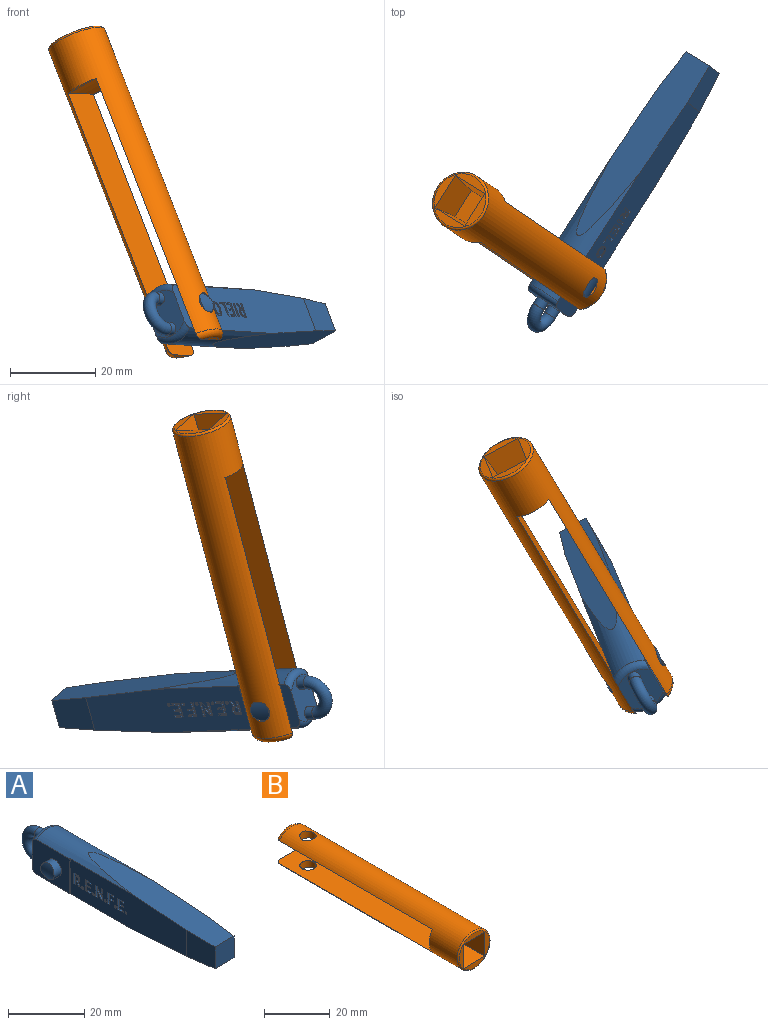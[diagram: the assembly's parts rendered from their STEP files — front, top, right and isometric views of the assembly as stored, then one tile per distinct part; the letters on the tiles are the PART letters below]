
ASSEMBLY  parts=2 mates=1
PART A: 277 faces, bbox 14x74.8x15.2 mm
  f0: plane 42.99x11.2mm, normal (-1,0,0), area 431.2mm2, adj f2,f3,f6,f10,f11,f12,f125,f126
  f1: plane 42.99x11.2mm, normal (1,0,0), area 436.1mm2, adj f2,f3,f7,f9,f10,f12,f18,f19
  f2: cylinder r=7mm len=35.47mm, axis (0,-1,0), area 201.7mm2, adj f0,f1,f5,f6,f7,f8,f12,f16
  f3: cylinder r=7mm len=35.47mm, axis (0,-1,0), area 201.7mm2, adj f0,f1,f5,f6,f7,f8,f10,f17
  f4: plane 11x8.5mm, normal (0,1,0), area 69mm2, adj f5,f8,f16,f17,f274,f275
  f5: plane 14x11.12mm, normal (-1,0,0), area 134.8mm2, adj f2,f3,f4,f6,f15,f16,f17
  f6: plane 11.2x0.05mm, normal (0,-1,0), area 0.6mm2, adj f0,f2,f3,f5
  f7: plane 11.2x0.05mm, normal (0,-1,0), area 0.6mm2, adj f1,f2,f3,f8
  f8: plane 14x11.12mm, normal (1,0,0), area 134.8mm2, adj f2,f3,f4,f7,f14,f16,f17
  f9: plane 10.01x8.4mm, normal (1,-0.07,0), area 77.3mm2, adj f1,f10,f12,f13
  f10: plane 50.05x8.4mm, normal (0,-0.07,1), area 360.7mm2, adj f0,f1,f3,f9,f11,f13
  f11: plane 10.01x8.4mm, normal (-1,-0.07,0), area 77.3mm2, adj f0,f10,f12,f13
  f12: plane 50.05x8.4mm, normal (0,-0.07,-1), area 360.7mm2, adj f0,f1,f2,f9,f11,f13
  f13: plane 7x7mm, normal (0,-1,0), area 49mm2, adj f9,f10,f11,f12
  f14: cylinder r=2.5mm len=5mm, axis (-1,0,0), area 39.6mm2, adj f8,f273
  f15: cylinder r=2.5mm len=5mm, axis (-1,0,0), area 39.6mm2, adj f5,f272
  f16: torus R=5.5mm, axis (0,-1,0), area 21.9mm2, adj f2,f4,f5,f8
  f17: torus R=5.5mm, axis (0,-1,0), area 21.9mm2, adj f3,f4,f5,f8
  f18: plane 1.41x0.5mm, normal (0,0,-1), area 0.7mm2, adj f1,f19,f21,f22
  f19: plane 0.5x0.43mm, normal (0,1,0), area 0.2mm2, adj f1,f18,f20,f22
  f20: plane 1.41x0.5mm, normal (0,0,1), area 0.7mm2, adj f1,f19,f21,f22
  f21: plane 0.5x0.43mm, normal (0,-1,0), area 0.2mm2, adj f1,f18,f20,f22
  f22: plane 1.41x0.43mm, normal (1,0,0), area 0.6mm2, adj f18,f19,f20,f21
  f23: extruded ~0.55x0.5mm, area 0.3mm2, adj f1,f24,f42,f43
  f24: extruded ~0.75x0.5mm, area 0.4mm2, adj f1,f23,f25,f43
  f25: extruded ~0.5x0.02mm, area 0mm2, adj f1,f24,f26,f43
  f26: extruded ~0.73x0.5mm, area 0.4mm2, adj f1,f25,f27,f43
  f27: extruded ~0.55x0.5mm, area 0.3mm2, adj f1,f26,f28,f43
  f28: extruded ~0.5x0.43mm, area 0.3mm2, adj f1,f27,f29,f43
  f29: extruded ~0.54x0.5mm, area 0.3mm2, adj f1,f28,f30,f43
  f30: plane 0.5x0.47mm, normal (0,-1,0), area 0.2mm2, adj f1,f29,f31,f43
  f31: extruded ~0.5x0.3mm, area 0.2mm2, adj f1,f30,f32,f43
  f32: extruded ~0.5x0.25mm, area 0.2mm2, adj f1,f31,f33,f43
  f33: extruded ~0.5x0.4mm, area 0.2mm2, adj f1,f32,f34,f43
  f34: extruded ~0.56x0.5mm, area 0.3mm2, adj f1,f33,f35,f43
  f35: extruded ~0.5x0.02mm, area 0mm2, adj f1,f34,f36,f43
  f36: extruded ~0.57x0.5mm, area 0.3mm2, adj f1,f35,f37,f43
  f37: extruded ~0.5x0.4mm, area 0.2mm2, adj f1,f36,f38,f43
  f38: extruded ~0.5x0.25mm, area 0.2mm2, adj f1,f37,f39,f43
  f39: extruded ~0.5x0.3mm, area 0.2mm2, adj f1,f38,f40,f43
  f40: plane 0.5x0.47mm, normal (0,-1,0), area 0.2mm2, adj f1,f39,f41,f43
  f41: extruded ~0.54x0.5mm, area 0.3mm2, adj f1,f40,f42,f43
  f42: extruded ~0.5x0.43mm, area 0.3mm2, adj f1,f23,f41,f43
  f43: plane 3.57x1.36mm, normal (1,0,0), area 2.3mm2, adj f23,f24,f25,f26,f27,f28,f29,f30
  f44: plane 3.07x0.5mm, normal (0,-1,0), area 1.5mm2, adj f1,f45,f49,f50
  f45: plane 0.58x0.5mm, normal (0,0,-1), area 0.3mm2, adj f1,f44,f46,f50
  f46: plane 3.5x0.5mm, normal (0,1,0), area 1.7mm2, adj f1,f45,f47,f50
  f47: plane 2.19x0.5mm, normal (0,0,1), area 1.1mm2, adj f1,f46,f48,f50
  f48: plane 0.5x0.43mm, normal (0,-1,0), area 0.2mm2, adj f1,f47,f49,f50
  f49: plane 1.61x0.5mm, normal (0,0,-1), area 0.8mm2, adj f1,f44,f48,f50
  f50: plane 3.5x2.19mm, normal (1,0,0), area 2.7mm2, adj f44,f45,f46,f47,f48,f49
  f51: plane 0.5x0.39mm, normal (0,1,0), area 0.2mm2, adj f1,f52,f54,f55
  f52: plane 1.27x0.5mm, normal (0,0,1), area 0.6mm2, adj f1,f51,f53,f55
  f53: plane 0.5x0.39mm, normal (0,-1,0), area 0.2mm2, adj f1,f52,f54,f55
  f54: plane 1.27x0.5mm, normal (0,0,-1), area 0.6mm2, adj f1,f51,f53,f55
  f55: plane 1.27x0.39mm, normal (1,0,0), area 0.5mm2, adj f51,f52,f53,f54
  f56: plane 3.5x0.5mm, normal (0,-1,0), area 1.7mm2, adj f1,f57,f59,f60
  f57: plane 0.58x0.5mm, normal (0,0,-1), area 0.3mm2, adj f1,f56,f58,f60
  f58: plane 3.5x0.5mm, normal (0,1,0), area 1.7mm2, adj f1,f57,f59,f60
  f59: plane 0.58x0.5mm, normal (0,0,1), area 0.3mm2, adj f1,f56,f58,f60
  f60: plane 3.5x0.58mm, normal (1,0,0), area 2mm2, adj f56,f57,f58,f59
  f61: plane 0.5x0.43mm, normal (0,-1,0), area 0.2mm2, adj f1,f62,f64,f65
  f62: plane 1.41x0.5mm, normal (0,0,-1), area 0.7mm2, adj f1,f61,f63,f65
  f63: plane 0.5x0.43mm, normal (0,1,0), area 0.2mm2, adj f1,f62,f64,f65
  f64: plane 1.41x0.5mm, normal (0,0,1), area 0.7mm2, adj f1,f61,f63,f65
  f65: plane 1.41x0.43mm, normal (1,0,0), area 0.6mm2, adj f61,f62,f63,f64
  f66: plane 3.5x0.5mm, normal (0,-1,0), area 1.7mm2, adj f1,f67,f69,f70
  f67: plane 0.57x0.5mm, normal (0,0,-1), area 0.3mm2, adj f1,f66,f68,f70
  f68: plane 3.5x0.5mm, normal (0,1,0), area 1.7mm2, adj f1,f67,f69,f70
  f69: plane 0.57x0.5mm, normal (0,0,1), area 0.3mm2, adj f1,f66,f68,f70
  f70: plane 3.5x0.57mm, normal (1,0,0), area 2mm2, adj f66,f67,f68,f69
  f71: extruded ~0.5x0.03mm, area 0mm2, adj f1,f72,f97,f98
  f72: plane 1.27x0.66mm, normal (0,0.89,0.46), area 0.7mm2, adj f1,f71,f73,f98
  f73: plane 0.6x0.5mm, normal (0,0,1), area 0.3mm2, adj f1,f72,f74,f98
  f74: plane 1.38x0.8mm, normal (0,-0.87,-0.5), area 0.8mm2, adj f1,f73,f75,f98
  f75: extruded ~0.5x0.46mm, area 0.3mm2, adj f1,f74,f76,f98
  f76: extruded ~0.5x0.02mm, area 0mm2, adj f1,f75,f77,f98
  f77: extruded ~0.65x0.5mm, area 0.3mm2, adj f1,f76,f78,f98
  f78: extruded ~0.5x0.45mm, area 0.2mm2, adj f1,f77,f79,f98
  f79: extruded ~0.5x0.34mm, area 0.2mm2, adj f1,f78,f80,f98
  f80: extruded ~0.5x0.39mm, area 0.2mm2, adj f1,f79,f81,f98
  f81: extruded ~0.5x0.44mm, area 0.2mm2, adj f1,f80,f82,f98
  f82: plane 0.5x0.24mm, normal (0,0,-1), area 0.1mm2, adj f1,f81,f83,f98
  f83: plane 0.5x0.43mm, normal (0,1,0), area 0.2mm2, adj f1,f82,f84,f98
  f84: plane 0.5x0.23mm, normal (0,0,1), area 0.1mm2, adj f1,f83,f85,f98
  f85: extruded ~0.5x0.35mm, area 0.2mm2, adj f1,f84,f86,f98
  f86: extruded ~0.5x0.21mm, area 0.1mm2, adj f1,f85,f87,f98
  f87: extruded ~0.5x0.21mm, area 0.1mm2, adj f1,f86,f88,f98
  f88: extruded ~0.5x0.2mm, area 0.1mm2, adj f1,f87,f89,f98
  f89: extruded ~0.5x0.36mm, area 0.2mm2, adj f1,f88,f90,f98
  f90: extruded ~0.5x0.23mm, area 0.1mm2, adj f1,f89,f91,f98
  f91: extruded ~0.5x0.11mm, area 0.1mm2, adj f1,f90,f92,f98
  f92: extruded ~0.5x0.08mm, area 0mm2, adj f1,f91,f93,f98
  f93: extruded ~0.5x0.21mm, area 0.1mm2, adj f1,f92,f94,f98
  f94: plane 0.5x0.32mm, normal (0,0,-1), area 0.2mm2, adj f1,f93,f95,f98
  f95: plane 0.5x0.42mm, normal (0,1,0), area 0.2mm2, adj f1,f94,f96,f98
  f96: plane 0.5x0.27mm, normal (0,0,1), area 0.1mm2, adj f1,f95,f97,f98
  f97: extruded ~0.5x0.05mm, area 0mm2, adj f1,f71,f96,f98
  f98: plane 3.5x1.61mm, normal (1,0,0), area 2.4mm2, adj f71,f72,f73,f74,f75,f76,f77,f78
  f99: plane 3.5x0.5mm, normal (0,1,0), area 1.7mm2, adj f1,f100,f102,f103
  f100: plane 0.58x0.5mm, normal (0,0,1), area 0.3mm2, adj f1,f99,f101,f103
  f101: plane 3.5x0.5mm, normal (0,-1,0), area 1.7mm2, adj f1,f100,f102,f103
  f102: plane 0.58x0.5mm, normal (0,0,-1), area 0.3mm2, adj f1,f99,f101,f103
  f103: plane 3.5x0.58mm, normal (1,0,0), area 2mm2, adj f99,f100,f101,f102
  f104: extruded ~0.55x0.5mm, area 0.3mm2, adj f1,f105,f123,f124
  f105: extruded ~0.5x0.43mm, area 0.3mm2, adj f1,f104,f106,f124
  f106: extruded ~0.54x0.5mm, area 0.3mm2, adj f1,f105,f107,f124
  f107: plane 0.5x0.47mm, normal (0,1,0), area 0.2mm2, adj f1,f106,f108,f124
  f108: extruded ~0.5x0.3mm, area 0.2mm2, adj f1,f107,f109,f124
  f109: extruded ~0.5x0.25mm, area 0.2mm2, adj f1,f108,f110,f124
  f110: extruded ~0.5x0.4mm, area 0.2mm2, adj f1,f109,f111,f124
  f111: extruded ~0.58x0.5mm, area 0.3mm2, adj f1,f110,f112,f124
  f112: extruded ~0.5x0.02mm, area 0mm2, adj f1,f111,f113,f124
  f113: extruded ~0.56x0.5mm, area 0.3mm2, adj f1,f112,f114,f124
  f114: extruded ~0.5x0.4mm, area 0.2mm2, adj f1,f113,f115,f124
  f115: extruded ~0.5x0.25mm, area 0.2mm2, adj f1,f114,f116,f124
  f116: extruded ~0.5x0.3mm, area 0.2mm2, adj f1,f115,f117,f124
  f117: plane 0.5x0.47mm, normal (0,1,0), area 0.2mm2, adj f1,f116,f118,f124
  f118: extruded ~0.54x0.5mm, area 0.3mm2, adj f1,f117,f119,f124
  f119: extruded ~0.5x0.43mm, area 0.3mm2, adj f1,f118,f120,f124
  f120: extruded ~0.55x0.5mm, area 0.3mm2, adj f1,f119,f121,f124
  f121: extruded ~0.73x0.5mm, area 0.4mm2, adj f1,f120,f122,f124
  f122: extruded ~0.5x0.02mm, area 0mm2, adj f1,f121,f123,f124
  f123: extruded ~0.75x0.5mm, area 0.4mm2, adj f1,f104,f122,f124
  f124: plane 3.57x1.36mm, normal (1,0,0), area 2.2mm2, adj f104,f105,f106,f107,f108,f109,f110,f111
  f125: extruded ~0.5x0.24mm, area 0.1mm2, adj f0,f126,f132,f133
  f126: extruded ~0.5x0.24mm, area 0.1mm2, adj f0,f125,f127,f133
  f127: extruded ~0.5x0.24mm, area 0.1mm2, adj f0,f126,f128,f133
  f128: extruded ~0.5x0.24mm, area 0.1mm2, adj f0,f127,f129,f133
  f129: extruded ~0.5x0.24mm, area 0.1mm2, adj f0,f128,f130,f133
  f130: extruded ~0.5x0.24mm, area 0.1mm2, adj f0,f129,f131,f133
  f131: extruded ~0.5x0.24mm, area 0.1mm2, adj f0,f130,f132,f133
  f132: extruded ~0.5x0.24mm, area 0.1mm2, adj f0,f125,f131,f133
  f133: plane 0.68x0.68mm, normal (-1,0,0), area 0.4mm2, adj f125,f126,f127,f128,f129,f130,f131,f132
  f134: plane 0.5x0.39mm, normal (0,-1,0), area 0.2mm2, adj f0,f135,f137,f138
  f135: plane 1.27x0.5mm, normal (0,0,1), area 0.6mm2, adj f0,f134,f136,f138
  f136: plane 0.5x0.39mm, normal (0,1,0), area 0.2mm2, adj f0,f135,f137,f138
  f137: plane 1.27x0.5mm, normal (0,0,-1), area 0.6mm2, adj f0,f134,f136,f138
  f138: plane 1.27x0.39mm, normal (-1,0,0), area 0.5mm2, adj f134,f135,f136,f137
  f139: plane 3.5x0.5mm, normal (0,1,0), area 1.7mm2, adj f0,f140,f142,f143
  f140: plane 0.58x0.5mm, normal (0,0,-1), area 0.3mm2, adj f0,f139,f141,f143
  f141: plane 3.5x0.5mm, normal (0,-1,0), area 1.7mm2, adj f0,f140,f142,f143
  f142: plane 0.58x0.5mm, normal (0,0,1), area 0.3mm2, adj f0,f139,f141,f143
  f143: plane 3.5x0.58mm, normal (-1,0,0), area 2mm2, adj f139,f140,f141,f142
  f144: plane 0.5x0.39mm, normal (0,-1,0), area 0.2mm2, adj f0,f145,f147,f148
  f145: plane 1.27x0.5mm, normal (0,0,1), area 0.6mm2, adj f0,f144,f146,f148
  f146: plane 0.5x0.39mm, normal (0,1,0), area 0.2mm2, adj f0,f145,f147,f148
  f147: plane 1.27x0.5mm, normal (0,0,-1), area 0.6mm2, adj f0,f144,f146,f148
  f148: plane 1.27x0.39mm, normal (-1,0,0), area 0.5mm2, adj f144,f145,f146,f147
  f149: plane 1.41x0.5mm, normal (0,0,-1), area 0.7mm2, adj f0,f150,f152,f153
  f150: plane 0.5x0.43mm, normal (0,-1,0), area 0.2mm2, adj f0,f149,f151,f153
  f151: plane 1.41x0.5mm, normal (0,0,1), area 0.7mm2, adj f0,f150,f152,f153
  f152: plane 0.5x0.43mm, normal (0,1,0), area 0.2mm2, adj f0,f149,f151,f153
  f153: plane 1.41x0.43mm, normal (-1,0,0), area 0.6mm2, adj f149,f150,f151,f152
  f154: plane 0.5x0.43mm, normal (0,1,0), area 0.2mm2, adj f0,f155,f157,f158
  f155: plane 1.41x0.5mm, normal (0,0,-1), area 0.7mm2, adj f0,f154,f156,f158
  f156: plane 0.5x0.43mm, normal (0,-1,0), area 0.2mm2, adj f0,f155,f157,f158
  f157: plane 1.41x0.5mm, normal (0,0,1), area 0.7mm2, adj f0,f154,f156,f158
  f158: plane 1.41x0.43mm, normal (-1,0,0), area 0.6mm2, adj f154,f155,f156,f157
  f159: extruded ~0.5x0.24mm, area 0.1mm2, adj f0,f160,f166,f167
  f160: extruded ~0.5x0.24mm, area 0.1mm2, adj f0,f159,f161,f167
  f161: extruded ~0.5x0.24mm, area 0.1mm2, adj f0,f160,f162,f167
  f162: extruded ~0.5x0.24mm, area 0.1mm2, adj f0,f161,f163,f167
  f163: extruded ~0.5x0.24mm, area 0.1mm2, adj f0,f162,f164,f167
  f164: extruded ~0.5x0.24mm, area 0.1mm2, adj f0,f163,f165,f167
  f165: extruded ~0.5x0.24mm, area 0.1mm2, adj f0,f164,f166,f167
  f166: extruded ~0.5x0.24mm, area 0.1mm2, adj f0,f159,f165,f167
  f167: plane 0.68x0.68mm, normal (-1,0,0), area 0.4mm2, adj f159,f160,f161,f162,f163,f164,f165,f166
  f168: extruded ~0.5x0.24mm, area 0.1mm2, adj f0,f169,f175,f176
  f169: extruded ~0.5x0.24mm, area 0.1mm2, adj f0,f168,f170,f176
  f170: extruded ~0.5x0.24mm, area 0.1mm2, adj f0,f169,f171,f176
  f171: extruded ~0.5x0.24mm, area 0.1mm2, adj f0,f170,f172,f176
  f172: extruded ~0.5x0.24mm, area 0.1mm2, adj f0,f171,f173,f176
  f173: extruded ~0.5x0.24mm, area 0.1mm2, adj f0,f172,f174,f176
  f174: extruded ~0.5x0.24mm, area 0.1mm2, adj f0,f173,f175,f176
  f175: extruded ~0.5x0.24mm, area 0.1mm2, adj f0,f168,f174,f176
  f176: plane 0.68x0.68mm, normal (-1,0,0), area 0.4mm2, adj f168,f169,f170,f171,f172,f173,f174,f175
  f177: plane 0.5x0.43mm, normal (0,1,0), area 0.2mm2, adj f0,f178,f180,f181
  f178: plane 1.41x0.5mm, normal (0,0,-1), area 0.7mm2, adj f0,f177,f179,f181
  f179: plane 0.5x0.43mm, normal (0,-1,0), area 0.2mm2, adj f0,f178,f180,f181
  f180: plane 1.41x0.5mm, normal (0,0,1), area 0.7mm2, adj f0,f177,f179,f181
  f181: plane 1.41x0.43mm, normal (-1,0,0), area 0.6mm2, adj f177,f178,f179,f180
  f182: extruded ~0.5x0.24mm, area 0.1mm2, adj f0,f183,f189,f190
  f183: extruded ~0.5x0.24mm, area 0.1mm2, adj f0,f182,f184,f190
  f184: extruded ~0.5x0.24mm, area 0.1mm2, adj f0,f183,f185,f190
  f185: extruded ~0.5x0.24mm, area 0.1mm2, adj f0,f184,f186,f190
  f186: extruded ~0.5x0.24mm, area 0.1mm2, adj f0,f185,f187,f190
  f187: extruded ~0.5x0.24mm, area 0.1mm2, adj f0,f186,f188,f190
  f188: extruded ~0.5x0.24mm, area 0.1mm2, adj f0,f187,f189,f190
  f189: extruded ~0.5x0.24mm, area 0.1mm2, adj f0,f182,f188,f190
  f190: plane 0.68x0.68mm, normal (-1,0,0), area 0.4mm2, adj f182,f183,f184,f185,f186,f187,f188,f189
  f191: plane 1.41x0.5mm, normal (0,0,-1), area 0.7mm2, adj f0,f192,f194,f195
  f192: plane 0.5x0.43mm, normal (0,-1,0), area 0.2mm2, adj f0,f191,f193,f195
  f193: plane 1.41x0.5mm, normal (0,0,1), area 0.7mm2, adj f0,f192,f194,f195
  f194: plane 0.5x0.43mm, normal (0,1,0), area 0.2mm2, adj f0,f191,f193,f195
  f195: plane 1.41x0.43mm, normal (-1,0,0), area 0.6mm2, adj f191,f192,f193,f194
  f196: plane 0.5x0.43mm, normal (0,1,0), area 0.2mm2, adj f0,f197,f199,f200
  f197: plane 1.41x0.5mm, normal (0,0,-1), area 0.7mm2, adj f0,f196,f198,f200
  f198: plane 0.5x0.43mm, normal (0,-1,0), area 0.2mm2, adj f0,f197,f199,f200
  f199: plane 1.41x0.5mm, normal (0,0,1), area 0.7mm2, adj f0,f196,f198,f200
  f200: plane 1.41x0.43mm, normal (-1,0,0), area 0.6mm2, adj f196,f197,f198,f199
  f201: plane 0.5x0.39mm, normal (0,-1,0), area 0.2mm2, adj f0,f202,f204,f205
  f202: plane 1.27x0.5mm, normal (0,0,1), area 0.6mm2, adj f0,f201,f203,f205
  f203: plane 0.5x0.39mm, normal (0,1,0), area 0.2mm2, adj f0,f202,f204,f205
  f204: plane 1.27x0.5mm, normal (0,0,-1), area 0.6mm2, adj f0,f201,f203,f205
  f205: plane 1.27x0.39mm, normal (-1,0,0), area 0.5mm2, adj f201,f202,f203,f204
  f206: plane 1.75x0.5mm, normal (0,-1,0), area 0.9mm2, adj f0,f207,f213,f214
  f207: plane 0.5x0.38mm, normal (0,0,-1), area 0.2mm2, adj f0,f206,f208,f214
  f208: plane 1.41x0.8mm, normal (0,0.87,-0.49), area 0.8mm2, adj f0,f207,f209,f214
  f209: plane 1.09x0.5mm, normal (0,-1,0), area 0.5mm2, adj f0,f208,f210,f214
  f210: plane 2.07x1.18mm, normal (0,-0.87,0.49), area 1.2mm2, adj f0,f209,f211,f214
  f211: plane 0.58x0.5mm, normal (0,0,1), area 0.3mm2, adj f0,f210,f212,f214
  f212: plane 3.5x0.5mm, normal (0,1,0), area 1.7mm2, adj f0,f211,f213,f214
  f213: plane 0.58x0.5mm, normal (0,0,-1), area 0.3mm2, adj f0,f206,f212,f214
  f214: plane 3.5x1.76mm, normal (-1,0,0), area 3.4mm2, adj f206,f207,f208,f209,f210,f211,f212,f213
  f215: plane 3.5x0.5mm, normal (0,-1,0), area 1.7mm2, adj f0,f216,f218,f219
  f216: plane 0.58x0.5mm, normal (0,0,1), area 0.3mm2, adj f0,f215,f217,f219
  f217: plane 3.5x0.5mm, normal (0,1,0), area 1.7mm2, adj f0,f216,f218,f219
  f218: plane 0.58x0.5mm, normal (0,0,-1), area 0.3mm2, adj f0,f215,f217,f219
  f219: plane 3.5x0.58mm, normal (-1,0,0), area 2mm2, adj f215,f216,f217,f218
  f220: plane 3.5x0.5mm, normal (0,1,0), area 1.7mm2, adj f0,f221,f223,f224
  f221: plane 0.58x0.5mm, normal (0,0,-1), area 0.3mm2, adj f0,f220,f222,f224
  f222: plane 3.5x0.5mm, normal (0,-1,0), area 1.7mm2, adj f0,f221,f223,f224
  f223: plane 0.58x0.5mm, normal (0,0,1), area 0.3mm2, adj f0,f220,f222,f224
  f224: plane 3.5x0.58mm, normal (-1,0,0), area 2mm2, adj f220,f221,f222,f223
  f225: extruded ~0.5x0.24mm, area 0.1mm2, adj f0,f226,f232,f233
  f226: extruded ~0.5x0.24mm, area 0.1mm2, adj f0,f225,f227,f233
  f227: extruded ~0.5x0.24mm, area 0.1mm2, adj f0,f226,f228,f233
  f228: extruded ~0.5x0.24mm, area 0.1mm2, adj f0,f227,f229,f233
  f229: extruded ~0.5x0.24mm, area 0.1mm2, adj f0,f228,f230,f233
  f230: extruded ~0.5x0.24mm, area 0.1mm2, adj f0,f229,f231,f233
  f231: extruded ~0.5x0.24mm, area 0.1mm2, adj f0,f230,f232,f233
  f232: extruded ~0.5x0.24mm, area 0.1mm2, adj f0,f225,f231,f233
  f233: plane 0.68x0.68mm, normal (-1,0,0), area 0.4mm2, adj f225,f226,f227,f228,f229,f230,f231,f232
  f234: plane 3.5x0.5mm, normal (0,1,0), area 1.7mm2, adj f0,f235,f237,f238
  f235: plane 0.57x0.5mm, normal (0,0,-1), area 0.3mm2, adj f0,f234,f236,f238
  f236: plane 3.5x0.5mm, normal (0,-1,0), area 1.7mm2, adj f0,f235,f237,f238
  f237: plane 0.57x0.5mm, normal (0,0,1), area 0.3mm2, adj f0,f234,f236,f238
  f238: plane 3.5x0.57mm, normal (-1,0,0), area 2mm2, adj f234,f235,f236,f237
  f239: extruded ~0.5x0.03mm, area 0mm2, adj f0,f240,f265,f266
  f240: plane 1.27x0.66mm, normal (0,-0.89,0.46), area 0.7mm2, adj f0,f239,f241,f266
  f241: plane 0.6x0.5mm, normal (0,0,1), area 0.3mm2, adj f0,f240,f242,f266
  f242: plane 1.38x0.8mm, normal (0,0.87,-0.5), area 0.8mm2, adj f0,f241,f243,f266
  f243: extruded ~0.5x0.46mm, area 0.3mm2, adj f0,f242,f244,f266
  f244: extruded ~0.5x0.02mm, area 0mm2, adj f0,f243,f245,f266
  f245: extruded ~0.65x0.5mm, area 0.3mm2, adj f0,f244,f246,f266
  f246: extruded ~0.5x0.45mm, area 0.2mm2, adj f0,f245,f247,f266
  f247: extruded ~0.5x0.34mm, area 0.2mm2, adj f0,f246,f248,f266
  f248: extruded ~0.5x0.39mm, area 0.2mm2, adj f0,f247,f249,f266
  f249: extruded ~0.5x0.44mm, area 0.2mm2, adj f0,f248,f250,f266
  f250: plane 0.5x0.24mm, normal (0,0,-1), area 0.1mm2, adj f0,f249,f251,f266
  f251: plane 0.5x0.43mm, normal (0,-1,0), area 0.2mm2, adj f0,f250,f252,f266
  f252: plane 0.5x0.23mm, normal (0,0,1), area 0.1mm2, adj f0,f251,f253,f266
  f253: extruded ~0.5x0.35mm, area 0.2mm2, adj f0,f252,f254,f266
  f254: extruded ~0.5x0.21mm, area 0.1mm2, adj f0,f253,f255,f266
  f255: extruded ~0.5x0.21mm, area 0.1mm2, adj f0,f254,f256,f266
  f256: extruded ~0.5x0.2mm, area 0.1mm2, adj f0,f255,f257,f266
  f257: extruded ~0.5x0.36mm, area 0.2mm2, adj f0,f256,f258,f266
  f258: extruded ~0.5x0.23mm, area 0.1mm2, adj f0,f257,f259,f266
  f259: extruded ~0.5x0.11mm, area 0.1mm2, adj f0,f258,f260,f266
  f260: extruded ~0.5x0.08mm, area 0mm2, adj f0,f259,f261,f266
  f261: extruded ~0.5x0.21mm, area 0.1mm2, adj f0,f260,f262,f266
  f262: plane 0.5x0.32mm, normal (0,0,-1), area 0.2mm2, adj f0,f261,f263,f266
  f263: plane 0.5x0.42mm, normal (0,-1,0), area 0.2mm2, adj f0,f262,f264,f266
  f264: plane 0.5x0.27mm, normal (0,0,1), area 0.1mm2, adj f0,f263,f265,f266
  f265: extruded ~0.5x0.05mm, area 0mm2, adj f0,f239,f264,f266
  f266: plane 3.5x1.61mm, normal (-1,0,0), area 2.4mm2, adj f239,f240,f241,f242,f243,f244,f245,f246
  f267: plane 3.5x0.5mm, normal (0,1,0), area 1.7mm2, adj f0,f268,f270,f271
  f268: plane 0.58x0.5mm, normal (0,0,-1), area 0.3mm2, adj f0,f267,f269,f271
  f269: plane 3.5x0.5mm, normal (0,-1,0), area 1.7mm2, adj f0,f268,f270,f271
  f270: plane 0.58x0.5mm, normal (0,0,1), area 0.3mm2, adj f0,f267,f269,f271
  f271: plane 3.5x0.58mm, normal (-1,0,0), area 2mm2, adj f267,f268,f269,f270
  f272: cylinder r=7mm len=5mm, axis (0,1,0), area 20mm2, adj f15
  f273: cylinder r=7mm len=5mm, axis (0,1,0), area 20mm2, adj f14
  f274: cylinder r=1.5mm len=3mm, axis (0,-1,0), area 18.8mm2, adj f4,f276
  f275: cylinder r=1.5mm len=3mm, axis (0,-1,0), area 18.8mm2, adj f4,f276
  f276: torus R=3.9mm, axis (1,0,0), area 115.5mm2, adj f274,f275
PART B: 19 faces, bbox 15.2x80x15.2 mm
  f0: plane 6.98x1.25mm, normal (0,1,0), area 6mm2, adj f13,f17
  f1: plane 8.5x1.44mm, normal (0,1,0), area 8.3mm2, adj f4,f15
  f2: plane 8.5x1.44mm, normal (0,1,0), area 8.3mm2, adj f4,f15
  f3: cylinder r=2.5mm len=5mm, axis (0,0,1), area 39.6mm2, adj f4,f13
  f4: cylinder r=7mm len=78mm, axis (0,-1,0), area 2184.9mm2, adj f1,f2,f3,f12,f13,f14,f16,f17
  f5: plane 13x13mm, normal (0,-1,0), area 51.7mm2, adj f7,f8,f9,f10,f16
  f6: plane 6.98x1.25mm, normal (0,1,0), area 6mm2, adj f12,f18
  f7: plane 10x9mm, normal (0,-0.09,1), area 81.6mm2, adj f5,f8,f10,f11
  f8: plane 10x9mm, normal (-1,-0.09,0), area 81.6mm2, adj f5,f7,f9,f11
  f9: plane 10x9mm, normal (0,-0.09,-1), area 81.6mm2, adj f5,f8,f10,f11
  f10: plane 10x9mm, normal (1,-0.09,0), area 81.6mm2, adj f5,f7,f9,f11
  f11: plane 7.25x7.25mm, normal (0,-1,0), area 52.6mm2, adj f7,f8,f9,f10
  f12: plane 67.76x11.12mm, normal (0,0,-1), area 731.9mm2, adj f4,f6,f14,f15,f18
  f13: plane 67.76x11.12mm, normal (0,0,1), area 731.9mm2, adj f0,f3,f4,f15,f17
  f14: cylinder r=2.5mm len=5mm, axis (0,0,1), area 39.6mm2, adj f4,f12
  f15: cylinder r=59.41mm len=11.12mm, axis (0,0,-1), area 94.7mm2, adj f1,f2,f12,f13
  f16: torus R=6.5mm, axis (0,-1,0), area 33.6mm2, adj f4,f5
  f17: torus R=5.5mm, axis (0,-1,0), area 25.9mm2, adj f0,f4,f13
  f18: torus R=5.5mm, axis (0,-1,0), area 25.9mm2, adj f4,f6,f12
PLACE A rot(axis=(0.94,-0.27,0.2),171.1deg) t=(85.69,-80.49,4.28)mm
PLACE B rot(axis=(-0.84,-0.46,0.3),124.5deg) t=(28.87,-112.89,71.15)mm
MATE revolute B.f3 <-> A.f14  axis (-0.77,0.47,-0.43) through (57.43,-131.92,8.11)mm
